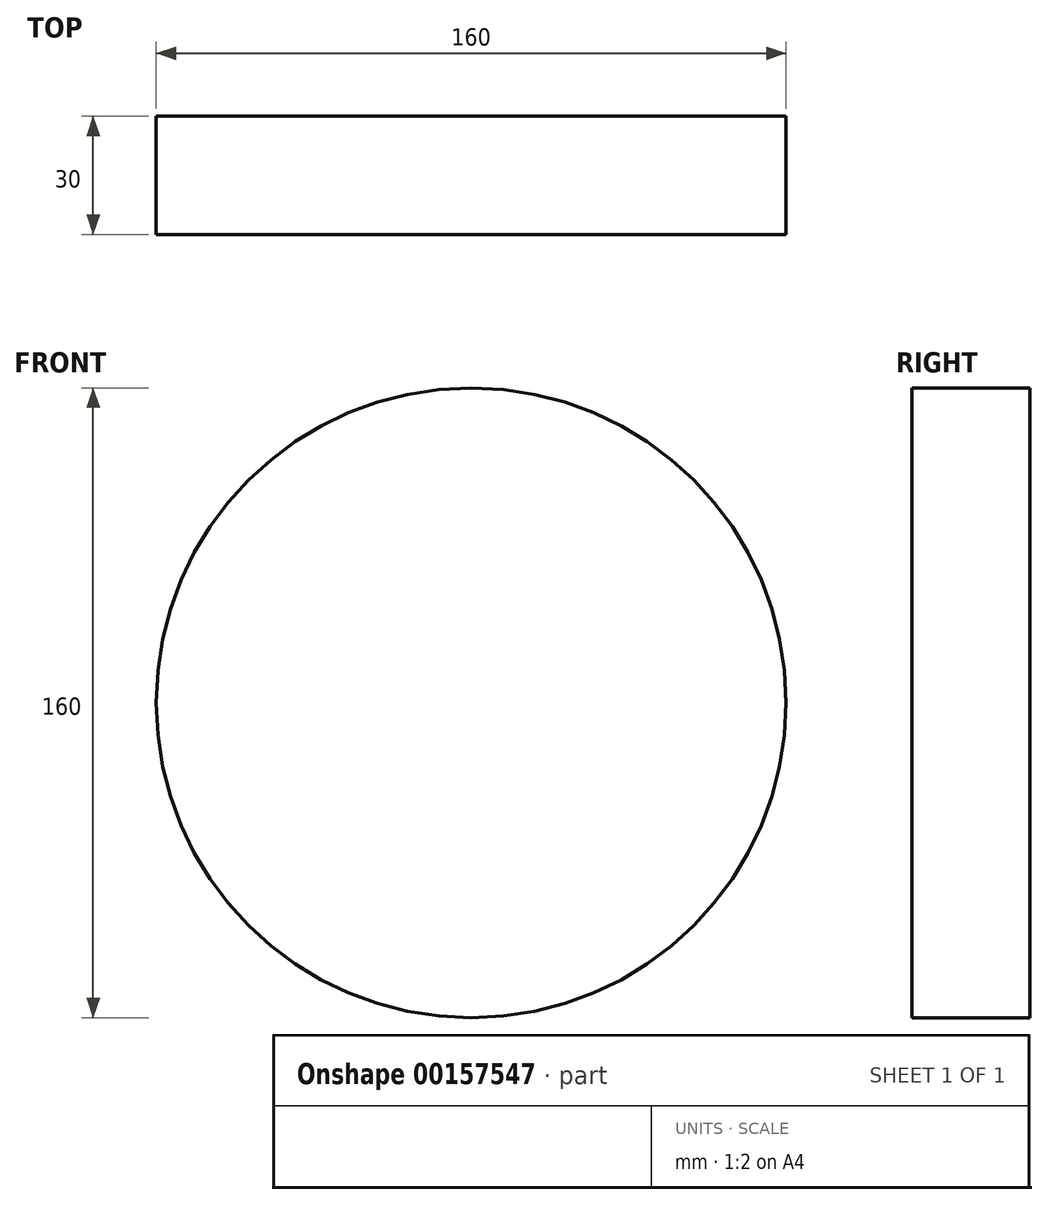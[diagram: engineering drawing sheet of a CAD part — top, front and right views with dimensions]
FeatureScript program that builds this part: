
annotation { "Feature Type Name" : "Feature", "Feature Type Description" : "" }
export const myFeature = defineFeature(function(context is Context, id is Id, definition is map)
    precondition{}
    {
        {
            var Q0;
            Q0=qCreatedBy(makeId("Front.planeOp"),FACE);
            var sketch = newSketch(context, id + "F0", { "sketchPlane" : qUnion([Q0])});
            skCircle(sketch, "E0", {"center": v(0, 0) * mm, "radius": 80 * mm});
            skSolve(sketch);
        }
        {
            var Q0;
            Q0=makeQuery(id+"F0.imprint","IMPRINT",FACE,{"disambiguationData":[TD([[makeQuery(id+"F0.imprint","IMPRINT",EDGE,{"derivedFrom":sQuery(id+"F0.wireOp",EDGE,"E0")}),1.0]])]});
            extrude(context, id + "F1", {"entities" : qUnion([Q0]), "depth" : 30 * mm});
        }
    });
